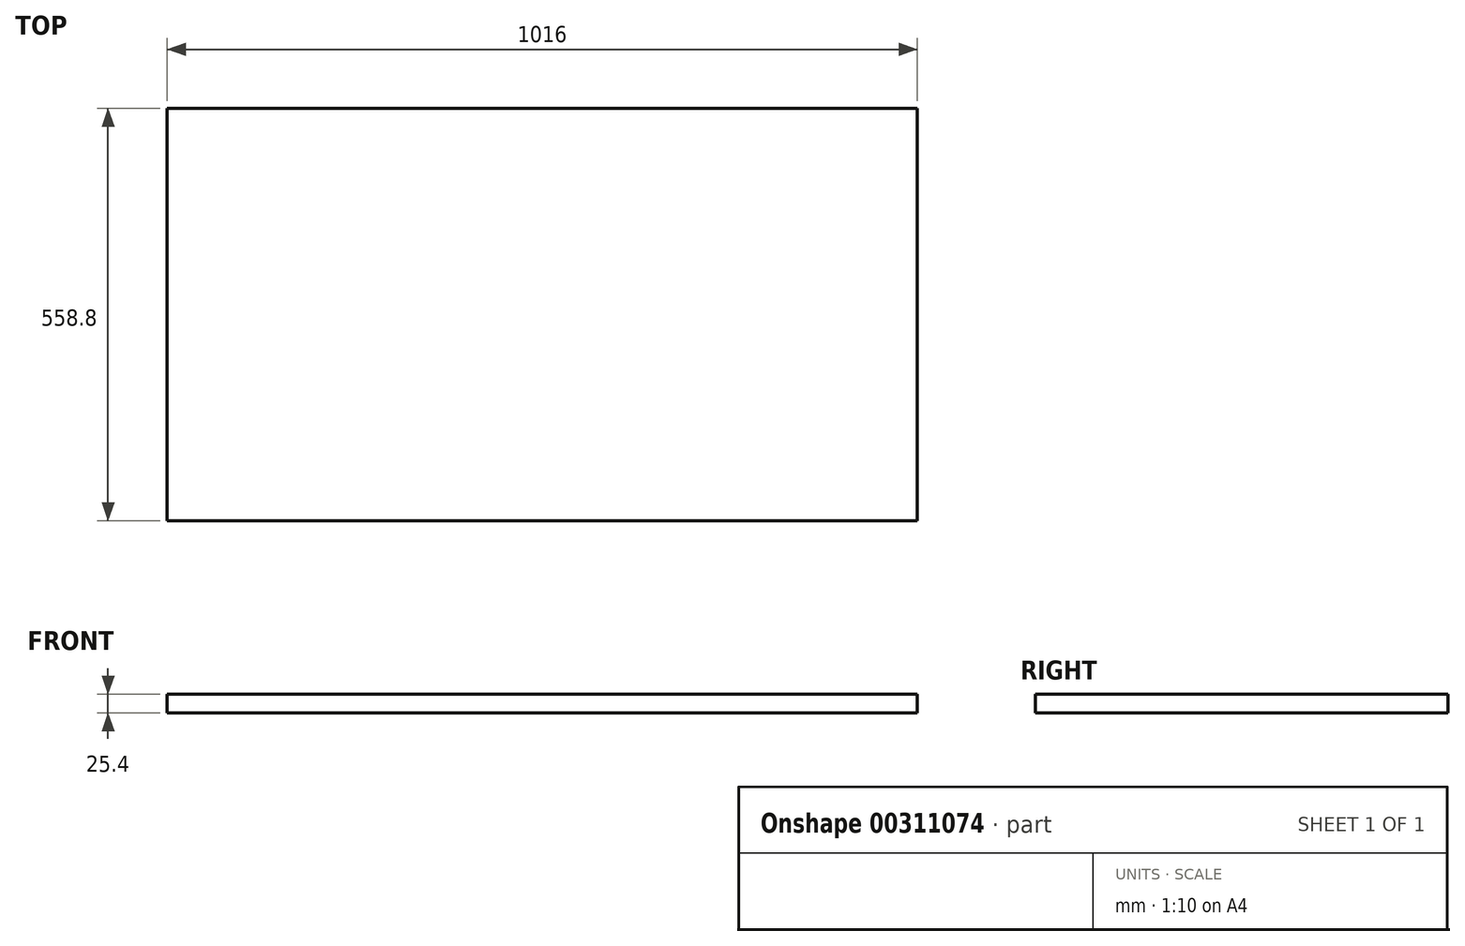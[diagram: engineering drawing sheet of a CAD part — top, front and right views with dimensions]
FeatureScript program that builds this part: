
annotation { "Feature Type Name" : "Feature", "Feature Type Description" : "" }
export const myFeature = defineFeature(function(context is Context, id is Id, definition is map)
    precondition{}
    {
        {
            var Q0;
            Q0=qCreatedBy(makeId("Top.planeOp"),FACE);
            var sketch = newSketch(context, id + "F0", { "sketchPlane" : qUnion([Q0])});
            skLineSegment(sketch, "E0.bottom", {"start": v(0, 0) * mm, "end": v(1016, 0) * mm});
            skLineSegment(sketch, "E0.top", {"start": v(0, 558.8) * mm, "end": v(1016, 558.8) * mm});
            skLineSegment(sketch, "E0.left", {"start": v(0, 0) * mm, "end": v(0, 558.8) * mm});
            skLineSegment(sketch, "E0.right", {"start": v(1016, 0) * mm, "end": v(1016, 558.8) * mm});
            skSolve(sketch);
        }
        {
            var Q0;
            Q0=makeQuery(id+"F0.imprint","IMPRINT",FACE,{"disambiguationData":[TD([[makeQuery(id+"F0.imprint","IMPRINT",EDGE,{"derivedFrom":sQuery(id+"F0.wireOp",EDGE,"E0.bottom")}),1.0]])]});
            extrude(context, id + "F1", {"entities" : qUnion([Q0]), "depth" : 25.4 * mm});
        }
    });
